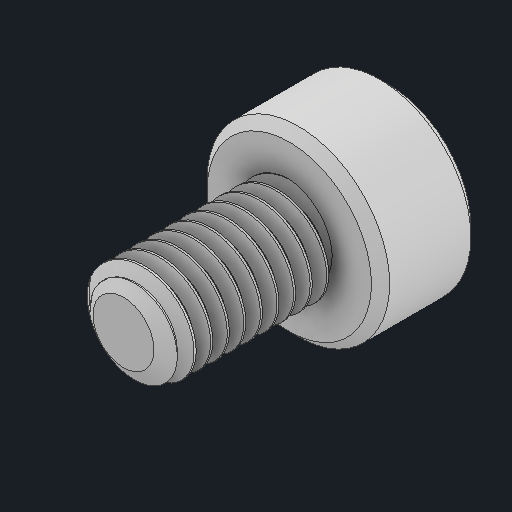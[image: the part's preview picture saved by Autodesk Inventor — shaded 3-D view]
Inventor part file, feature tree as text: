
AUTODESK INVENTOR PART (.ipt)
format: ipt  version: 2025 (Build 290162000, 162)  size: 496,640 bytes
history: native  units: in
note: dims shown in document units (in); Inventor stores cm internally (conversion verified against a paired STEP export)
features: chamfer x1
ambient origin geometry x8: Origin, YZ Plane, XZ Plane, XY Plane, X Axis, Y Axis, Z Axis, Center Point
bodies: Solid1 (feature_tree)
feature tree (1):
  chamfer  "Chamfer1"  [1 undecoded]
note: 1 required parameter value undecoded (feature->parameter linkage not recoverable at this tier; creation-order binding heuristic only, values carry confidence <= 0.55)
